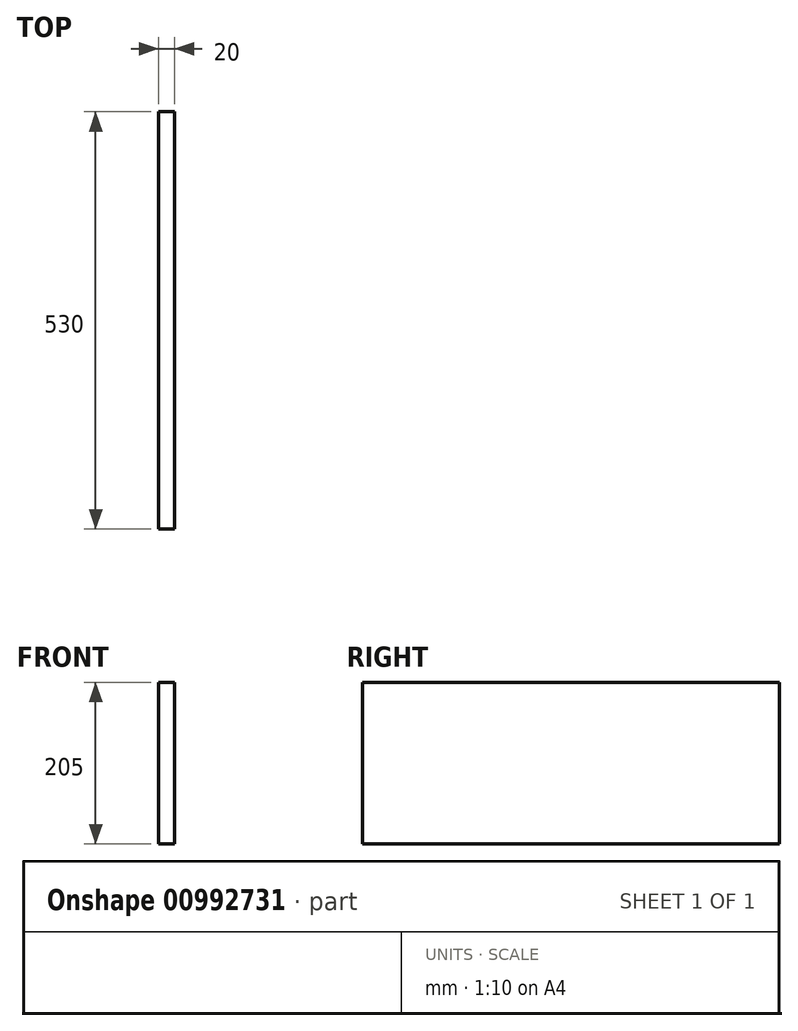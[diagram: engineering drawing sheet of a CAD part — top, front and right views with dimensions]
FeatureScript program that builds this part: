
annotation { "Feature Type Name" : "Feature", "Feature Type Description" : "" }
export const myFeature = defineFeature(function(context is Context, id is Id, definition is map)
    precondition{}
    {
        {
            var Q0;
            Q0=qCreatedBy(makeId("Top.planeOp"),FACE);
            var sketch = newSketch(context, id + "F0", { "sketchPlane" : qUnion([Q0])});
            skLineSegment(sketch, "E0.bottom", {"start": v(182.5, 265) * mm, "end": v(-182.5, 265) * mm});
            skLineSegment(sketch, "E0.top", {"start": v(182.5, -265) * mm, "end": v(-182.5, -265) * mm});
            skLineSegment(sketch, "E0.left", {"start": v(182.5, 265) * mm, "end": v(182.5, -265) * mm});
            skLineSegment(sketch, "E0.right", {"start": v(-182.5, 265) * mm, "end": v(-182.5, -265) * mm});
            skPoint(sketch, "E0.middle", {"position": v(0, 0) * mm});
            skSolve(sketch);
        }
        {
            var Q0;
            Q0=makeQuery(id+"F0.imprint","IMPRINT",FACE,{"disambiguationData":[TD([[makeQuery(id+"F0.imprint","IMPRINT",EDGE,{"derivedFrom":sQuery(id+"F0.wireOp",EDGE,"E0.bottom")}),1.0]])]});
            extrude(context, id + "F1", {"entities" : qUnion([Q0]), "depth" : 10 * mm, "offsetDistance" : 25 * mm});
        }
        {
            var Q0;
            Q0=makeQuery(id+"F1.opExtrude","CAP_FACE",FACE,{"disambiguationData":[OSD([sQuery(id+"F0.wireOp",EDGE,"E0.bottom"),sQuery(id+"F0.wireOp",EDGE,"E0.top"),sQuery(id+"F0.wireOp",EDGE,"E0.left"),sQuery(id+"F0.wireOp",EDGE,"E0.right")])],"isStart":false});
            var sketch = newSketch(context, id + "F2", { "sketchPlane" : qUnion([Q0])});
            skLineSegment(sketch, "E1.bottom", {"start": v(-182.5, 265) * mm, "end": v(-162.5, 265) * mm});
            skLineSegment(sketch, "E1.top", {"start": v(-182.5, -265) * mm, "end": v(-162.5, -265) * mm});
            skLineSegment(sketch, "E1.left", {"start": v(-182.5, 265) * mm, "end": v(-182.5, -265) * mm});
            skLineSegment(sketch, "E1.right", {"start": v(-162.5, 265) * mm, "end": v(-162.5, -265) * mm});
            skLineSegment(sketch, "E2.bottom", {"start": v(182.5, 265) * mm, "end": v(162.5, 265) * mm});
            skLineSegment(sketch, "E2.top", {"start": v(182.5, -265) * mm, "end": v(162.5, -265) * mm});
            skLineSegment(sketch, "E2.left", {"start": v(182.5, 265) * mm, "end": v(182.5, -265) * mm});
            skLineSegment(sketch, "E2.right", {"start": v(162.5, 265) * mm, "end": v(162.5, -265) * mm});
            skLineSegment(sketch, "E3.bottom", {"start": v(-162.5, -265) * mm, "end": v(162.5, -265) * mm});
            skLineSegment(sketch, "E3.top", {"start": v(-162.5, -245) * mm, "end": v(162.5, -245) * mm});
            skLineSegment(sketch, "E3.left", {"start": v(-162.5, -265) * mm, "end": v(-162.5, -245) * mm});
            skLineSegment(sketch, "E3.right", {"start": v(162.5, -265) * mm, "end": v(162.5, -245) * mm});
            skLineSegment(sketch, "E4.bottom", {"start": v(162.5, 265) * mm, "end": v(-162.5, 265) * mm});
            skLineSegment(sketch, "E4.top", {"start": v(162.5, 245) * mm, "end": v(-162.5, 245) * mm});
            skLineSegment(sketch, "E4.left", {"start": v(162.5, 265) * mm, "end": v(162.5, 245) * mm});
            skLineSegment(sketch, "E4.right", {"start": v(-162.5, 265) * mm, "end": v(-162.5, 245) * mm});
            skSolve(sketch);
        }
        {
            var Q0;
            Q0=makeQuery(id+"F2.imprint","IMPRINT",FACE,{"disambiguationData":[TD([[makeQuery(id+"F2.imprint","IMPRINT",EDGE,{"derivedFrom":sQuery(id+"F2.wireOp",EDGE,"E1.bottom")}),1.0]])]});
            var Q1;
            Q1=makeQuery(id+"F2.imprint","IMPRINT",FACE,{"disambiguationData":[TD([[makeQuery(id+"F2.imprint","IMPRINT",EDGE,{"derivedFrom":sQuery(id+"F2.wireOp",EDGE,"E4.bottom")}),1.0]])]});
            var Q2;
            Q2=makeQuery(id+"F2.imprint","IMPRINT",FACE,{"disambiguationData":[TD([[makeQuery(id+"F2.imprint","IMPRINT",EDGE,{"derivedFrom":sQuery(id+"F2.wireOp",EDGE,"E2.bottom")}),1.0]])]});
            var Q3;
            Q3=makeQuery(id+"F2.imprint","IMPRINT",FACE,{"disambiguationData":[TD([[makeQuery(id+"F2.imprint","IMPRINT",EDGE,{"derivedFrom":sQuery(id+"F2.wireOp",EDGE,"E3.bottom")}),-1.0]])]});
            extrude(context, id + "F3", {"entities" : qUnion([Q0, Q1, Q2, Q3]), "operationType" : NewBodyOperationType.ADD, "depth" : 195 * mm, "offsetDistance" : 25 * mm});
        }
        {
            var Q0;
            Q0=makeQuery(id+"F3.opExtrude","CAP_FACE",FACE,{"disambiguationData":[OSD([sQuery(id+"F2.wireOp",EDGE,"E1.bottom"),sQuery(id+"F2.wireOp",EDGE,"E1.top"),sQuery(id+"F2.wireOp",EDGE,"E1.left"),sQuery(id+"F2.wireOp",EDGE,"E1.right"),sQuery(id+"F2.wireOp",EDGE,"E2.bottom"),sQuery(id+"F2.wireOp",EDGE,"E2.top"),sQuery(id+"F2.wireOp",EDGE,"E2.left"),sQuery(id+"F2.wireOp",EDGE,"E2.right"),sQuery(id+"F2.wireOp",EDGE,"E3.bottom"),sQuery(id+"F2.wireOp",EDGE,"E3.top"),sQuery(id+"F2.wireOp",EDGE,"E4.bottom"),sQuery(id+"F2.wireOp",EDGE,"E4.top")])],"isStart":false});
            var sketch = newSketch(context, id + "F4", { "sketchPlane" : qUnion([Q0])});
            skLineSegment(sketch, "E5.bottom", {"start": v(182.5, 265) * mm, "end": v(-162.5, 265) * mm});
            skLineSegment(sketch, "E5.top", {"start": v(182.5, -265) * mm, "end": v(-162.5, -265) * mm});
            skLineSegment(sketch, "E5.left", {"start": v(182.5, 265) * mm, "end": v(182.5, -265) * mm});
            skLineSegment(sketch, "E5.right", {"start": v(-162.5, 265) * mm, "end": v(-162.5, -265) * mm});
            skSolve(sketch);
        }
        {
            var Q0;
            {var subQ2=sQuery(id+"F4.wireOp",EDGE,"E5.bottom");Q0=makeQuery(id+"F4.imprint","IMPRINT",FACE,{"disambiguationData":[TD([[makeQuery(id+"F4.imprint","IMPRINT",EDGE,{"derivedFrom":subQ2}),1.0]])]});}
            var Q1;
            Q1=makeQuery(id+"F4.imprint","IMPRINT",FACE,{"disambiguationData":[TD([[makeQuery(id+"F4.imprint","IMPRINT",EDGE,{"derivedFrom":makeQuery(id+"F3.opExtrude","CAP_EDGE",EDGE,{"disambiguationData":[OSD([sQuery(id+"F2.wireOp",EDGE,"E2.right")])],"isStart":false})}),-1.0]])]});
            extrude(context, id + "F5", {"entities" : qUnion([Q0, Q1]), "operationType" : NewBodyOperationType.REMOVE, "endBound" : BoundingType.THROUGH_ALL, "oppositeDirection" : true, "depth" : 25 * mm, "offsetDistance" : 25 * mm});
        }
    });
